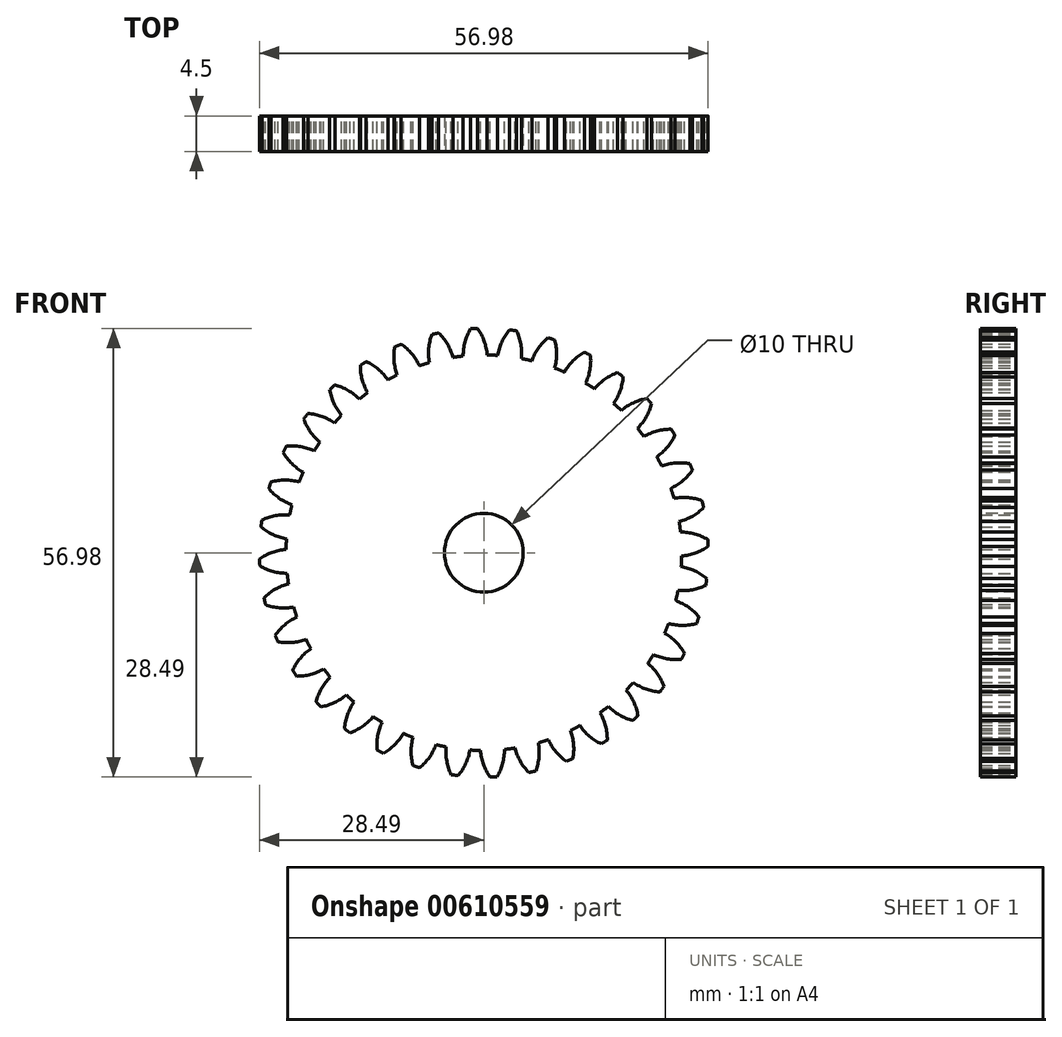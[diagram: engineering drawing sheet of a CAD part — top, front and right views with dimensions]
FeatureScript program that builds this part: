
annotation { "Feature Type Name" : "Feature", "Feature Type Description" : "" }
export const myFeature = defineFeature(function(context is Context, id is Id, definition is map)
    precondition{}
    {
        {
            var Q0;
            Q0=qCreatedBy(makeId("Front.planeOp"),FACE);
            var sketch = newSketch(context, id + "F0", { "sketchPlane" : qUnion([Q0])});
            skCircle(sketch, "E0", {"center": v(0, 0) * mm, "radius": 83.75 * mm});
            skCircle(sketch, "E1", {"center": v(0, 0) * mm, "radius": 90 * mm, "construction": true});
            skCircle(sketch, "E2", {"center": v(0, 0) * mm, "radius": 95 * mm, "construction": true});
            skLineSegment(sketch, "E3", {"start": v(0, 0) * mm, "end": v(0, 175.5) * mm, "construction": true});
            skLineSegment(sketch, "E4", {"start": v(0, 0) * mm, "end": v(-7.83, 179.33) * mm, "construction": true});
            skLineSegment(sketch, "E5", {"start": v(0, 90) * mm, "end": v(-217.65, 90) * mm, "construction": true});
            skLineSegment(sketch, "E6", {"start": v(0, 90) * mm, "end": v(-200.71, 16.95) * mm, "construction": true});
            skCircle(sketch, "E7", {"center": v(0, 0) * mm, "radius": 84.57 * mm, "construction": true});
            skCircle(sketch, "E8", {"center": v(0, 90) * mm, "radius": 22.5 * mm, "construction": true});
            skArc(sketch, "E9", {"start": v(0, 90) * mm, "mid": v(-1.18, 92.57) * mm, "end": v(-2.66, 94.96) * mm});
            skArc(sketch, "E10", {"start": v(1.43, 83.74) * mm, "mid": v(0.94, 86.92) * mm, "end": v(0, 90) * mm});
            skArc(sketch, "E11.MirrorCS", {"start": v(-8.72, 83.3) * mm, "mid": v(-8.5, 86.5) * mm, "end": v(-7.84, 89.66) * mm});
            skArc(sketch, "E12.MirrorCS", {"start": v(-7.84, 89.66) * mm, "mid": v(-6.9, 92.32) * mm, "end": v(-5.62, 94.83) * mm});
            skArc(sketch, "E13", {"start": v(-5.62, 94.83) * mm, "mid": v(-4.14, 94.9) * mm, "end": v(-2.66, 94.96) * mm});
            skCircle(sketch, "E14", {"center": v(0, 0) * mm, "radius": 25 * mm});
            skSolve(sketch);
        }
        {
            var Q0;
            Q0=makeQuery(id+"F0.imprint","IMPRINT",FACE,{"disambiguationData":[TD([[makeQuery(id+"F0.imprint","IMPRINT",EDGE,{"derivedFrom":sQuery(id+"F0.wireOp",EDGE,"E9")}),1.0]])]});
            var Q1;
            {var subQ0=sQuery(id+"F0.wireOp",EDGE,"E0");var subQ1=makeQuery(id+"F0.imprint","INTERSECT",VERTEX,{"derivedFrom":[subQ0,sQuery(id+"F0.wireOp",EDGE,"E10")]});Q1=makeQuery(id+"F0.imprint","IMPRINT",FACE,{"disambiguationData":[TD([[makeQuery(id+"F0.imprint","IMPRINT",EDGE,{"disambiguationData":[TD([[subQ1,-1.0]])],"derivedFrom":subQ0}),1.0]])]});}
            var Q2;
            Q2=makeQuery(id+"F0.imprint","IMPRINT",FACE,{"disambiguationData":[TD([[makeQuery(id+"F0.imprint","IMPRINT",EDGE,{"derivedFrom":sQuery(id+"F0.wireOp",EDGE,"E14")}),1.0]])]});
            extrude(context, id + "F1", {"entities" : qUnion([Q0, Q1, Q2]), "depth" : 15 * mm, "offsetDistance" : 25.4 * mm});
        }
        {
            var Q0;
            Q0=makeQuery(id+"F1.opExtrude","SWEPT_BODY",BODY,{"disambiguationData":[OSD([sQuery(id+"F0.wireOp",EDGE,"E0"),sQuery(id+"F0.wireOp",EDGE,"E9"),sQuery(id+"F0.wireOp",EDGE,"E10"),sQuery(id+"F0.wireOp",EDGE,"E11.MirrorCS"),sQuery(id+"F0.wireOp",EDGE,"E12.MirrorCS"),sQuery(id+"F0.wireOp",EDGE,"E13")])]});
            var Q1;
            Q1=makeQuery(id+"F1.opExtrude","SWEPT_FACE",FACE,{"disambiguationData":[OSD([sQuery(id+"F0.wireOp",EDGE,"E0")])]});
            circularPattern(context, id + "F2", {"entities" : qUnion([Q0]), "axis" : qUnion([Q1]), "angle" : 360 * degree, "instanceCount" : 36, "equalSpace" : true});
        }
        {
            var Q0;
            Q0=makeQuery(id+"F2.opPattern","COPY",BODY,{"derivedFrom":makeQuery(id+"F1.opExtrude","SWEPT_BODY",BODY,{"disambiguationData":[OSD([sQuery(id+"F0.wireOp",EDGE,"E0"),sQuery(id+"F0.wireOp",EDGE,"E9"),sQuery(id+"F0.wireOp",EDGE,"E10"),sQuery(id+"F0.wireOp",EDGE,"E11.MirrorCS"),sQuery(id+"F0.wireOp",EDGE,"E12.MirrorCS"),sQuery(id+"F0.wireOp",EDGE,"E13")])]}),"instanceName":"11"});
            var Q1;
            Q1=makeQuery(id+"F2.opPattern","COPY",BODY,{"derivedFrom":makeQuery(id+"F1.opExtrude","SWEPT_BODY",BODY,{"disambiguationData":[OSD([sQuery(id+"F0.wireOp",EDGE,"E0"),sQuery(id+"F0.wireOp",EDGE,"E9"),sQuery(id+"F0.wireOp",EDGE,"E10"),sQuery(id+"F0.wireOp",EDGE,"E11.MirrorCS"),sQuery(id+"F0.wireOp",EDGE,"E12.MirrorCS"),sQuery(id+"F0.wireOp",EDGE,"E13")])]}),"instanceName":"1"});
            var Q2;
            Q2=makeQuery(id+"F2.opPattern","COPY",BODY,{"derivedFrom":makeQuery(id+"F1.opExtrude","SWEPT_BODY",BODY,{"disambiguationData":[OSD([sQuery(id+"F0.wireOp",EDGE,"E0"),sQuery(id+"F0.wireOp",EDGE,"E9"),sQuery(id+"F0.wireOp",EDGE,"E10"),sQuery(id+"F0.wireOp",EDGE,"E11.MirrorCS"),sQuery(id+"F0.wireOp",EDGE,"E12.MirrorCS"),sQuery(id+"F0.wireOp",EDGE,"E13")])]}),"instanceName":"22"});
            var Q3;
            Q3=makeQuery(id+"F2.opPattern","COPY",BODY,{"derivedFrom":makeQuery(id+"F1.opExtrude","SWEPT_BODY",BODY,{"disambiguationData":[OSD([sQuery(id+"F0.wireOp",EDGE,"E0"),sQuery(id+"F0.wireOp",EDGE,"E9"),sQuery(id+"F0.wireOp",EDGE,"E10"),sQuery(id+"F0.wireOp",EDGE,"E11.MirrorCS"),sQuery(id+"F0.wireOp",EDGE,"E12.MirrorCS"),sQuery(id+"F0.wireOp",EDGE,"E13")])]}),"instanceName":"28"});
            var Q4;
            Q4=makeQuery(id+"F2.opPattern","COPY",BODY,{"derivedFrom":makeQuery(id+"F1.opExtrude","SWEPT_BODY",BODY,{"disambiguationData":[OSD([sQuery(id+"F0.wireOp",EDGE,"E0"),sQuery(id+"F0.wireOp",EDGE,"E9"),sQuery(id+"F0.wireOp",EDGE,"E10"),sQuery(id+"F0.wireOp",EDGE,"E11.MirrorCS"),sQuery(id+"F0.wireOp",EDGE,"E12.MirrorCS"),sQuery(id+"F0.wireOp",EDGE,"E13")])]}),"instanceName":"32"});
            var Q5;
            Q5=makeQuery(id+"F2.opPattern","COPY",BODY,{"derivedFrom":makeQuery(id+"F1.opExtrude","SWEPT_BODY",BODY,{"disambiguationData":[OSD([sQuery(id+"F0.wireOp",EDGE,"E0"),sQuery(id+"F0.wireOp",EDGE,"E9"),sQuery(id+"F0.wireOp",EDGE,"E10"),sQuery(id+"F0.wireOp",EDGE,"E11.MirrorCS"),sQuery(id+"F0.wireOp",EDGE,"E12.MirrorCS"),sQuery(id+"F0.wireOp",EDGE,"E13")])]}),"instanceName":"31"});
            var Q6;
            Q6=makeQuery(id+"F2.opPattern","COPY",BODY,{"derivedFrom":makeQuery(id+"F1.opExtrude","SWEPT_BODY",BODY,{"disambiguationData":[OSD([sQuery(id+"F0.wireOp",EDGE,"E0"),sQuery(id+"F0.wireOp",EDGE,"E9"),sQuery(id+"F0.wireOp",EDGE,"E10"),sQuery(id+"F0.wireOp",EDGE,"E11.MirrorCS"),sQuery(id+"F0.wireOp",EDGE,"E12.MirrorCS"),sQuery(id+"F0.wireOp",EDGE,"E13")])]}),"instanceName":"10"});
            var Q7;
            Q7=makeQuery(id+"F2.opPattern","COPY",BODY,{"derivedFrom":makeQuery(id+"F1.opExtrude","SWEPT_BODY",BODY,{"disambiguationData":[OSD([sQuery(id+"F0.wireOp",EDGE,"E0"),sQuery(id+"F0.wireOp",EDGE,"E9"),sQuery(id+"F0.wireOp",EDGE,"E10"),sQuery(id+"F0.wireOp",EDGE,"E11.MirrorCS"),sQuery(id+"F0.wireOp",EDGE,"E12.MirrorCS"),sQuery(id+"F0.wireOp",EDGE,"E13")])]}),"instanceName":"17"});
            var Q8;
            Q8=makeQuery(id+"F2.opPattern","COPY",BODY,{"derivedFrom":makeQuery(id+"F1.opExtrude","SWEPT_BODY",BODY,{"disambiguationData":[OSD([sQuery(id+"F0.wireOp",EDGE,"E0"),sQuery(id+"F0.wireOp",EDGE,"E9"),sQuery(id+"F0.wireOp",EDGE,"E10"),sQuery(id+"F0.wireOp",EDGE,"E11.MirrorCS"),sQuery(id+"F0.wireOp",EDGE,"E12.MirrorCS"),sQuery(id+"F0.wireOp",EDGE,"E13")])]}),"instanceName":"23"});
            var Q9;
            Q9=makeQuery(id+"F2.opPattern","COPY",BODY,{"derivedFrom":makeQuery(id+"F1.opExtrude","SWEPT_BODY",BODY,{"disambiguationData":[OSD([sQuery(id+"F0.wireOp",EDGE,"E0"),sQuery(id+"F0.wireOp",EDGE,"E9"),sQuery(id+"F0.wireOp",EDGE,"E10"),sQuery(id+"F0.wireOp",EDGE,"E11.MirrorCS"),sQuery(id+"F0.wireOp",EDGE,"E12.MirrorCS"),sQuery(id+"F0.wireOp",EDGE,"E13")])]}),"instanceName":"18"});
            var Q10;
            Q10=makeQuery(id+"F2.opPattern","COPY",BODY,{"derivedFrom":makeQuery(id+"F1.opExtrude","SWEPT_BODY",BODY,{"disambiguationData":[OSD([sQuery(id+"F0.wireOp",EDGE,"E0"),sQuery(id+"F0.wireOp",EDGE,"E9"),sQuery(id+"F0.wireOp",EDGE,"E10"),sQuery(id+"F0.wireOp",EDGE,"E11.MirrorCS"),sQuery(id+"F0.wireOp",EDGE,"E12.MirrorCS"),sQuery(id+"F0.wireOp",EDGE,"E13")])]}),"instanceName":"29"});
            var Q11;
            Q11=makeQuery(id+"F2.opPattern","COPY",BODY,{"derivedFrom":makeQuery(id+"F1.opExtrude","SWEPT_BODY",BODY,{"disambiguationData":[OSD([sQuery(id+"F0.wireOp",EDGE,"E0"),sQuery(id+"F0.wireOp",EDGE,"E9"),sQuery(id+"F0.wireOp",EDGE,"E10"),sQuery(id+"F0.wireOp",EDGE,"E11.MirrorCS"),sQuery(id+"F0.wireOp",EDGE,"E12.MirrorCS"),sQuery(id+"F0.wireOp",EDGE,"E13")])]}),"instanceName":"30"});
            var Q12;
            Q12=makeQuery(id+"F2.opPattern","COPY",BODY,{"derivedFrom":makeQuery(id+"F1.opExtrude","SWEPT_BODY",BODY,{"disambiguationData":[OSD([sQuery(id+"F0.wireOp",EDGE,"E0"),sQuery(id+"F0.wireOp",EDGE,"E9"),sQuery(id+"F0.wireOp",EDGE,"E10"),sQuery(id+"F0.wireOp",EDGE,"E11.MirrorCS"),sQuery(id+"F0.wireOp",EDGE,"E12.MirrorCS"),sQuery(id+"F0.wireOp",EDGE,"E13")])]}),"instanceName":"15"});
            var Q13;
            Q13=makeQuery(id+"F2.opPattern","COPY",BODY,{"derivedFrom":makeQuery(id+"F1.opExtrude","SWEPT_BODY",BODY,{"disambiguationData":[OSD([sQuery(id+"F0.wireOp",EDGE,"E0"),sQuery(id+"F0.wireOp",EDGE,"E9"),sQuery(id+"F0.wireOp",EDGE,"E10"),sQuery(id+"F0.wireOp",EDGE,"E11.MirrorCS"),sQuery(id+"F0.wireOp",EDGE,"E12.MirrorCS"),sQuery(id+"F0.wireOp",EDGE,"E13")])]}),"instanceName":"33"});
            var Q14;
            Q14=makeQuery(id+"F2.opPattern","COPY",BODY,{"derivedFrom":makeQuery(id+"F1.opExtrude","SWEPT_BODY",BODY,{"disambiguationData":[OSD([sQuery(id+"F0.wireOp",EDGE,"E0"),sQuery(id+"F0.wireOp",EDGE,"E9"),sQuery(id+"F0.wireOp",EDGE,"E10"),sQuery(id+"F0.wireOp",EDGE,"E11.MirrorCS"),sQuery(id+"F0.wireOp",EDGE,"E12.MirrorCS"),sQuery(id+"F0.wireOp",EDGE,"E13")])]}),"instanceName":"12"});
            var Q15;
            Q15=makeQuery(id+"F2.opPattern","COPY",BODY,{"derivedFrom":makeQuery(id+"F1.opExtrude","SWEPT_BODY",BODY,{"disambiguationData":[OSD([sQuery(id+"F0.wireOp",EDGE,"E0"),sQuery(id+"F0.wireOp",EDGE,"E9"),sQuery(id+"F0.wireOp",EDGE,"E10"),sQuery(id+"F0.wireOp",EDGE,"E11.MirrorCS"),sQuery(id+"F0.wireOp",EDGE,"E12.MirrorCS"),sQuery(id+"F0.wireOp",EDGE,"E13")])]}),"instanceName":"21"});
            var Q16;
            Q16=makeQuery(id+"F2.opPattern","COPY",BODY,{"derivedFrom":makeQuery(id+"F1.opExtrude","SWEPT_BODY",BODY,{"disambiguationData":[OSD([sQuery(id+"F0.wireOp",EDGE,"E0"),sQuery(id+"F0.wireOp",EDGE,"E9"),sQuery(id+"F0.wireOp",EDGE,"E10"),sQuery(id+"F0.wireOp",EDGE,"E11.MirrorCS"),sQuery(id+"F0.wireOp",EDGE,"E12.MirrorCS"),sQuery(id+"F0.wireOp",EDGE,"E13")])]}),"instanceName":"34"});
            var Q17;
            Q17=makeQuery(id+"F2.opPattern","COPY",BODY,{"derivedFrom":makeQuery(id+"F1.opExtrude","SWEPT_BODY",BODY,{"disambiguationData":[OSD([sQuery(id+"F0.wireOp",EDGE,"E0"),sQuery(id+"F0.wireOp",EDGE,"E9"),sQuery(id+"F0.wireOp",EDGE,"E10"),sQuery(id+"F0.wireOp",EDGE,"E11.MirrorCS"),sQuery(id+"F0.wireOp",EDGE,"E12.MirrorCS"),sQuery(id+"F0.wireOp",EDGE,"E13")])]}),"instanceName":"16"});
            var Q18;
            Q18=makeQuery(id+"F1.opExtrude","SWEPT_BODY",BODY,{"disambiguationData":[OSD([sQuery(id+"F0.wireOp",EDGE,"E0"),sQuery(id+"F0.wireOp",EDGE,"E9"),sQuery(id+"F0.wireOp",EDGE,"E10"),sQuery(id+"F0.wireOp",EDGE,"E11.MirrorCS"),sQuery(id+"F0.wireOp",EDGE,"E12.MirrorCS"),sQuery(id+"F0.wireOp",EDGE,"E13")])]});
            var Q19;
            Q19=makeQuery(id+"F2.opPattern","COPY",BODY,{"derivedFrom":makeQuery(id+"F1.opExtrude","SWEPT_BODY",BODY,{"disambiguationData":[OSD([sQuery(id+"F0.wireOp",EDGE,"E0"),sQuery(id+"F0.wireOp",EDGE,"E9"),sQuery(id+"F0.wireOp",EDGE,"E10"),sQuery(id+"F0.wireOp",EDGE,"E11.MirrorCS"),sQuery(id+"F0.wireOp",EDGE,"E12.MirrorCS"),sQuery(id+"F0.wireOp",EDGE,"E13")])]}),"instanceName":"24"});
            var Q20;
            Q20=makeQuery(id+"F2.opPattern","COPY",BODY,{"derivedFrom":makeQuery(id+"F1.opExtrude","SWEPT_BODY",BODY,{"disambiguationData":[OSD([sQuery(id+"F0.wireOp",EDGE,"E0"),sQuery(id+"F0.wireOp",EDGE,"E9"),sQuery(id+"F0.wireOp",EDGE,"E10"),sQuery(id+"F0.wireOp",EDGE,"E11.MirrorCS"),sQuery(id+"F0.wireOp",EDGE,"E12.MirrorCS"),sQuery(id+"F0.wireOp",EDGE,"E13")])]}),"instanceName":"27"});
            var Q21;
            Q21=makeQuery(id+"F2.opPattern","COPY",BODY,{"derivedFrom":makeQuery(id+"F1.opExtrude","SWEPT_BODY",BODY,{"disambiguationData":[OSD([sQuery(id+"F0.wireOp",EDGE,"E0"),sQuery(id+"F0.wireOp",EDGE,"E9"),sQuery(id+"F0.wireOp",EDGE,"E10"),sQuery(id+"F0.wireOp",EDGE,"E11.MirrorCS"),sQuery(id+"F0.wireOp",EDGE,"E12.MirrorCS"),sQuery(id+"F0.wireOp",EDGE,"E13")])]}),"instanceName":"20"});
            var Q22;
            Q22=makeQuery(id+"F2.opPattern","COPY",BODY,{"derivedFrom":makeQuery(id+"F1.opExtrude","SWEPT_BODY",BODY,{"disambiguationData":[OSD([sQuery(id+"F0.wireOp",EDGE,"E0"),sQuery(id+"F0.wireOp",EDGE,"E9"),sQuery(id+"F0.wireOp",EDGE,"E10"),sQuery(id+"F0.wireOp",EDGE,"E11.MirrorCS"),sQuery(id+"F0.wireOp",EDGE,"E12.MirrorCS"),sQuery(id+"F0.wireOp",EDGE,"E13")])]}),"instanceName":"14"});
            var Q23;
            Q23=makeQuery(id+"F2.opPattern","COPY",BODY,{"derivedFrom":makeQuery(id+"F1.opExtrude","SWEPT_BODY",BODY,{"disambiguationData":[OSD([sQuery(id+"F0.wireOp",EDGE,"E0"),sQuery(id+"F0.wireOp",EDGE,"E9"),sQuery(id+"F0.wireOp",EDGE,"E10"),sQuery(id+"F0.wireOp",EDGE,"E11.MirrorCS"),sQuery(id+"F0.wireOp",EDGE,"E12.MirrorCS"),sQuery(id+"F0.wireOp",EDGE,"E13")])]}),"instanceName":"25"});
            var Q24;
            Q24=makeQuery(id+"F2.opPattern","COPY",BODY,{"derivedFrom":makeQuery(id+"F1.opExtrude","SWEPT_BODY",BODY,{"disambiguationData":[OSD([sQuery(id+"F0.wireOp",EDGE,"E0"),sQuery(id+"F0.wireOp",EDGE,"E9"),sQuery(id+"F0.wireOp",EDGE,"E10"),sQuery(id+"F0.wireOp",EDGE,"E11.MirrorCS"),sQuery(id+"F0.wireOp",EDGE,"E12.MirrorCS"),sQuery(id+"F0.wireOp",EDGE,"E13")])]}),"instanceName":"26"});
            var Q25;
            Q25=makeQuery(id+"F2.opPattern","COPY",BODY,{"derivedFrom":makeQuery(id+"F1.opExtrude","SWEPT_BODY",BODY,{"disambiguationData":[OSD([sQuery(id+"F0.wireOp",EDGE,"E0"),sQuery(id+"F0.wireOp",EDGE,"E9"),sQuery(id+"F0.wireOp",EDGE,"E10"),sQuery(id+"F0.wireOp",EDGE,"E11.MirrorCS"),sQuery(id+"F0.wireOp",EDGE,"E12.MirrorCS"),sQuery(id+"F0.wireOp",EDGE,"E13")])]}),"instanceName":"35"});
            var Q26;
            Q26=makeQuery(id+"F2.opPattern","COPY",BODY,{"derivedFrom":makeQuery(id+"F1.opExtrude","SWEPT_BODY",BODY,{"disambiguationData":[OSD([sQuery(id+"F0.wireOp",EDGE,"E0"),sQuery(id+"F0.wireOp",EDGE,"E9"),sQuery(id+"F0.wireOp",EDGE,"E10"),sQuery(id+"F0.wireOp",EDGE,"E11.MirrorCS"),sQuery(id+"F0.wireOp",EDGE,"E12.MirrorCS"),sQuery(id+"F0.wireOp",EDGE,"E13")])]}),"instanceName":"9"});
            var Q27;
            Q27=makeQuery(id+"F2.opPattern","COPY",BODY,{"derivedFrom":makeQuery(id+"F1.opExtrude","SWEPT_BODY",BODY,{"disambiguationData":[OSD([sQuery(id+"F0.wireOp",EDGE,"E0"),sQuery(id+"F0.wireOp",EDGE,"E9"),sQuery(id+"F0.wireOp",EDGE,"E10"),sQuery(id+"F0.wireOp",EDGE,"E11.MirrorCS"),sQuery(id+"F0.wireOp",EDGE,"E12.MirrorCS"),sQuery(id+"F0.wireOp",EDGE,"E13")])]}),"instanceName":"19"});
            var Q28;
            Q28=makeQuery(id+"F2.opPattern","COPY",BODY,{"derivedFrom":makeQuery(id+"F1.opExtrude","SWEPT_BODY",BODY,{"disambiguationData":[OSD([sQuery(id+"F0.wireOp",EDGE,"E0"),sQuery(id+"F0.wireOp",EDGE,"E9"),sQuery(id+"F0.wireOp",EDGE,"E10"),sQuery(id+"F0.wireOp",EDGE,"E11.MirrorCS"),sQuery(id+"F0.wireOp",EDGE,"E12.MirrorCS"),sQuery(id+"F0.wireOp",EDGE,"E13")])]}),"instanceName":"6"});
            var Q29;
            Q29=makeQuery(id+"F2.opPattern","COPY",BODY,{"derivedFrom":makeQuery(id+"F1.opExtrude","SWEPT_BODY",BODY,{"disambiguationData":[OSD([sQuery(id+"F0.wireOp",EDGE,"E0"),sQuery(id+"F0.wireOp",EDGE,"E9"),sQuery(id+"F0.wireOp",EDGE,"E10"),sQuery(id+"F0.wireOp",EDGE,"E11.MirrorCS"),sQuery(id+"F0.wireOp",EDGE,"E12.MirrorCS"),sQuery(id+"F0.wireOp",EDGE,"E13")])]}),"instanceName":"3"});
            var Q30;
            Q30=makeQuery(id+"F2.opPattern","COPY",BODY,{"derivedFrom":makeQuery(id+"F1.opExtrude","SWEPT_BODY",BODY,{"disambiguationData":[OSD([sQuery(id+"F0.wireOp",EDGE,"E0"),sQuery(id+"F0.wireOp",EDGE,"E9"),sQuery(id+"F0.wireOp",EDGE,"E10"),sQuery(id+"F0.wireOp",EDGE,"E11.MirrorCS"),sQuery(id+"F0.wireOp",EDGE,"E12.MirrorCS"),sQuery(id+"F0.wireOp",EDGE,"E13")])]}),"instanceName":"13"});
            var Q31;
            Q31=makeQuery(id+"F2.opPattern","COPY",BODY,{"derivedFrom":makeQuery(id+"F1.opExtrude","SWEPT_BODY",BODY,{"disambiguationData":[OSD([sQuery(id+"F0.wireOp",EDGE,"E0"),sQuery(id+"F0.wireOp",EDGE,"E9"),sQuery(id+"F0.wireOp",EDGE,"E10"),sQuery(id+"F0.wireOp",EDGE,"E11.MirrorCS"),sQuery(id+"F0.wireOp",EDGE,"E12.MirrorCS"),sQuery(id+"F0.wireOp",EDGE,"E13")])]}),"instanceName":"7"});
            var Q32;
            Q32=makeQuery(id+"F2.opPattern","COPY",BODY,{"derivedFrom":makeQuery(id+"F1.opExtrude","SWEPT_BODY",BODY,{"disambiguationData":[OSD([sQuery(id+"F0.wireOp",EDGE,"E0"),sQuery(id+"F0.wireOp",EDGE,"E9"),sQuery(id+"F0.wireOp",EDGE,"E10"),sQuery(id+"F0.wireOp",EDGE,"E11.MirrorCS"),sQuery(id+"F0.wireOp",EDGE,"E12.MirrorCS"),sQuery(id+"F0.wireOp",EDGE,"E13")])]}),"instanceName":"5"});
            var Q33;
            Q33=makeQuery(id+"F2.opPattern","COPY",BODY,{"derivedFrom":makeQuery(id+"F1.opExtrude","SWEPT_BODY",BODY,{"disambiguationData":[OSD([sQuery(id+"F0.wireOp",EDGE,"E0"),sQuery(id+"F0.wireOp",EDGE,"E9"),sQuery(id+"F0.wireOp",EDGE,"E10"),sQuery(id+"F0.wireOp",EDGE,"E11.MirrorCS"),sQuery(id+"F0.wireOp",EDGE,"E12.MirrorCS"),sQuery(id+"F0.wireOp",EDGE,"E13")])]}),"instanceName":"8"});
            var Q34;
            Q34=makeQuery(id+"F2.opPattern","COPY",BODY,{"derivedFrom":makeQuery(id+"F1.opExtrude","SWEPT_BODY",BODY,{"disambiguationData":[OSD([sQuery(id+"F0.wireOp",EDGE,"E0"),sQuery(id+"F0.wireOp",EDGE,"E9"),sQuery(id+"F0.wireOp",EDGE,"E10"),sQuery(id+"F0.wireOp",EDGE,"E11.MirrorCS"),sQuery(id+"F0.wireOp",EDGE,"E12.MirrorCS"),sQuery(id+"F0.wireOp",EDGE,"E13")])]}),"instanceName":"4"});
            var Q35;
            Q35=makeQuery(id+"F2.opPattern","COPY",BODY,{"derivedFrom":makeQuery(id+"F1.opExtrude","SWEPT_BODY",BODY,{"disambiguationData":[OSD([sQuery(id+"F0.wireOp",EDGE,"E0"),sQuery(id+"F0.wireOp",EDGE,"E9"),sQuery(id+"F0.wireOp",EDGE,"E10"),sQuery(id+"F0.wireOp",EDGE,"E11.MirrorCS"),sQuery(id+"F0.wireOp",EDGE,"E12.MirrorCS"),sQuery(id+"F0.wireOp",EDGE,"E13")])]}),"instanceName":"2"});
            booleanBodies(context, id + "F3", {"operationType" : BooleanOperationType.UNION, "tools" : qUnion([Q0, Q1, Q2, Q3, Q4, Q5, Q6, Q7, Q8, Q9, Q10, Q11, Q12, Q13, Q14, Q15, Q16, Q17, Q18, Q19, Q20, Q21, Q22, Q23, Q24, Q25, Q26, Q27, Q28, Q29, Q30, Q31, Q32, Q33, Q34, Q35])});
        }
        {
            var Q0;
            Q0=makeQuery(id+"F2.opPattern","COPY",BODY,{"derivedFrom":makeQuery(id+"F1.opExtrude","SWEPT_BODY",BODY,{"disambiguationData":[OSD([sQuery(id+"F0.wireOp",EDGE,"E0"),sQuery(id+"F0.wireOp",EDGE,"E9"),sQuery(id+"F0.wireOp",EDGE,"E10"),sQuery(id+"F0.wireOp",EDGE,"E11.MirrorCS"),sQuery(id+"F0.wireOp",EDGE,"E12.MirrorCS"),sQuery(id+"F0.wireOp",EDGE,"E13")])]}),"instanceName":"11"});
            var Q1;
            Q1=sQuery(id+"F0.wireOp",VERTEX,"E0.center");
            transform(context, id + "F4", {"entities" : qUnion([Q0]), "transformType" : TransformType.SCALE_UNIFORMLY, "scale" : 0.3, "scalePoint" : qUnion([Q1]), "makeCopy" : false});
        }
        {
            var Q0;
            {var subQ0=makeQuery(id+"F1.opExtrude","CAP_FACE",FACE,{"disambiguationData":[OSD([sQuery(id+"F0.wireOp",EDGE,"E0"),sQuery(id+"F0.wireOp",EDGE,"E9"),sQuery(id+"F0.wireOp",EDGE,"E10"),sQuery(id+"F0.wireOp",EDGE,"E11.MirrorCS"),sQuery(id+"F0.wireOp",EDGE,"E12.MirrorCS"),sQuery(id+"F0.wireOp",EDGE,"E13")])],"isStart":false});Q0=makeQuery(id+"F3.opBoolean","MERGE",FACE,{"derivedFrom":[subQ0,makeQuery(id+"F2.opPattern","COPY",FACE,{"derivedFrom":subQ0,"instanceName":"1"}),makeQuery(id+"F2.opPattern","COPY",FACE,{"derivedFrom":subQ0,"instanceName":"2"}),makeQuery(id+"F2.opPattern","COPY",FACE,{"derivedFrom":subQ0,"instanceName":"3"}),makeQuery(id+"F2.opPattern","COPY",FACE,{"derivedFrom":subQ0,"instanceName":"4"}),makeQuery(id+"F2.opPattern","COPY",FACE,{"derivedFrom":subQ0,"instanceName":"5"}),makeQuery(id+"F2.opPattern","COPY",FACE,{"derivedFrom":subQ0,"instanceName":"6"}),makeQuery(id+"F2.opPattern","COPY",FACE,{"derivedFrom":subQ0,"instanceName":"7"}),makeQuery(id+"F2.opPattern","COPY",FACE,{"derivedFrom":subQ0,"instanceName":"8"}),makeQuery(id+"F2.opPattern","COPY",FACE,{"derivedFrom":subQ0,"instanceName":"9"}),makeQuery(id+"F2.opPattern","COPY",FACE,{"derivedFrom":subQ0,"instanceName":"10"}),makeQuery(id+"F2.opPattern","COPY",FACE,{"derivedFrom":subQ0,"instanceName":"11"}),makeQuery(id+"F2.opPattern","COPY",FACE,{"derivedFrom":subQ0,"instanceName":"12"}),makeQuery(id+"F2.opPattern","COPY",FACE,{"derivedFrom":subQ0,"instanceName":"13"}),makeQuery(id+"F2.opPattern","COPY",FACE,{"derivedFrom":subQ0,"instanceName":"14"}),makeQuery(id+"F2.opPattern","COPY",FACE,{"derivedFrom":subQ0,"instanceName":"15"}),makeQuery(id+"F2.opPattern","COPY",FACE,{"derivedFrom":subQ0,"instanceName":"16"}),makeQuery(id+"F2.opPattern","COPY",FACE,{"derivedFrom":subQ0,"instanceName":"17"}),makeQuery(id+"F2.opPattern","COPY",FACE,{"derivedFrom":subQ0,"instanceName":"18"}),makeQuery(id+"F2.opPattern","COPY",FACE,{"derivedFrom":subQ0,"instanceName":"19"}),makeQuery(id+"F2.opPattern","COPY",FACE,{"derivedFrom":subQ0,"instanceName":"20"}),makeQuery(id+"F2.opPattern","COPY",FACE,{"derivedFrom":subQ0,"instanceName":"21"}),makeQuery(id+"F2.opPattern","COPY",FACE,{"derivedFrom":subQ0,"instanceName":"22"}),makeQuery(id+"F2.opPattern","COPY",FACE,{"derivedFrom":subQ0,"instanceName":"23"}),makeQuery(id+"F2.opPattern","COPY",FACE,{"derivedFrom":subQ0,"instanceName":"24"}),makeQuery(id+"F2.opPattern","COPY",FACE,{"derivedFrom":subQ0,"instanceName":"25"}),makeQuery(id+"F2.opPattern","COPY",FACE,{"derivedFrom":subQ0,"instanceName":"26"}),makeQuery(id+"F2.opPattern","COPY",FACE,{"derivedFrom":subQ0,"instanceName":"27"}),makeQuery(id+"F2.opPattern","COPY",FACE,{"derivedFrom":subQ0,"instanceName":"28"}),makeQuery(id+"F2.opPattern","COPY",FACE,{"derivedFrom":subQ0,"instanceName":"29"}),makeQuery(id+"F2.opPattern","COPY",FACE,{"derivedFrom":subQ0,"instanceName":"30"}),makeQuery(id+"F2.opPattern","COPY",FACE,{"derivedFrom":subQ0,"instanceName":"31"}),makeQuery(id+"F2.opPattern","COPY",FACE,{"derivedFrom":subQ0,"instanceName":"32"}),makeQuery(id+"F2.opPattern","COPY",FACE,{"derivedFrom":subQ0,"instanceName":"33"}),makeQuery(id+"F2.opPattern","COPY",FACE,{"derivedFrom":subQ0,"instanceName":"34"}),makeQuery(id+"F2.opPattern","COPY",FACE,{"derivedFrom":subQ0,"instanceName":"35"})]});}
            var sketch = newSketch(context, id + "F5", { "sketchPlane" : qUnion([Q0])});
            skCircle(sketch, "E15", {"center": v(0, 0) * mm, "radius": 5 * mm});
            skSolve(sketch);
        }
        {
            var Q0;
            Q0=makeQuery(id+"F5.imprint","IMPRINT",FACE,{"disambiguationData":[TD([[makeQuery(id+"F5.imprint","IMPRINT",EDGE,{"derivedFrom":sQuery(id+"F5.wireOp",EDGE,"E15")}),1.0]])]});
            var Q1;
            Q1=sQuery(id+"F5.wireOp",EDGE,"E15");
            extrude(context, id + "F6", {"entities" : qUnion([Q0]), "operationType" : NewBodyOperationType.REMOVE, "surfaceEntities" : qUnion([Q1]), "oppositeDirection" : true, "depth" : 25.4 * mm, "offsetDistance" : 25.4 * mm});
        }
    });
